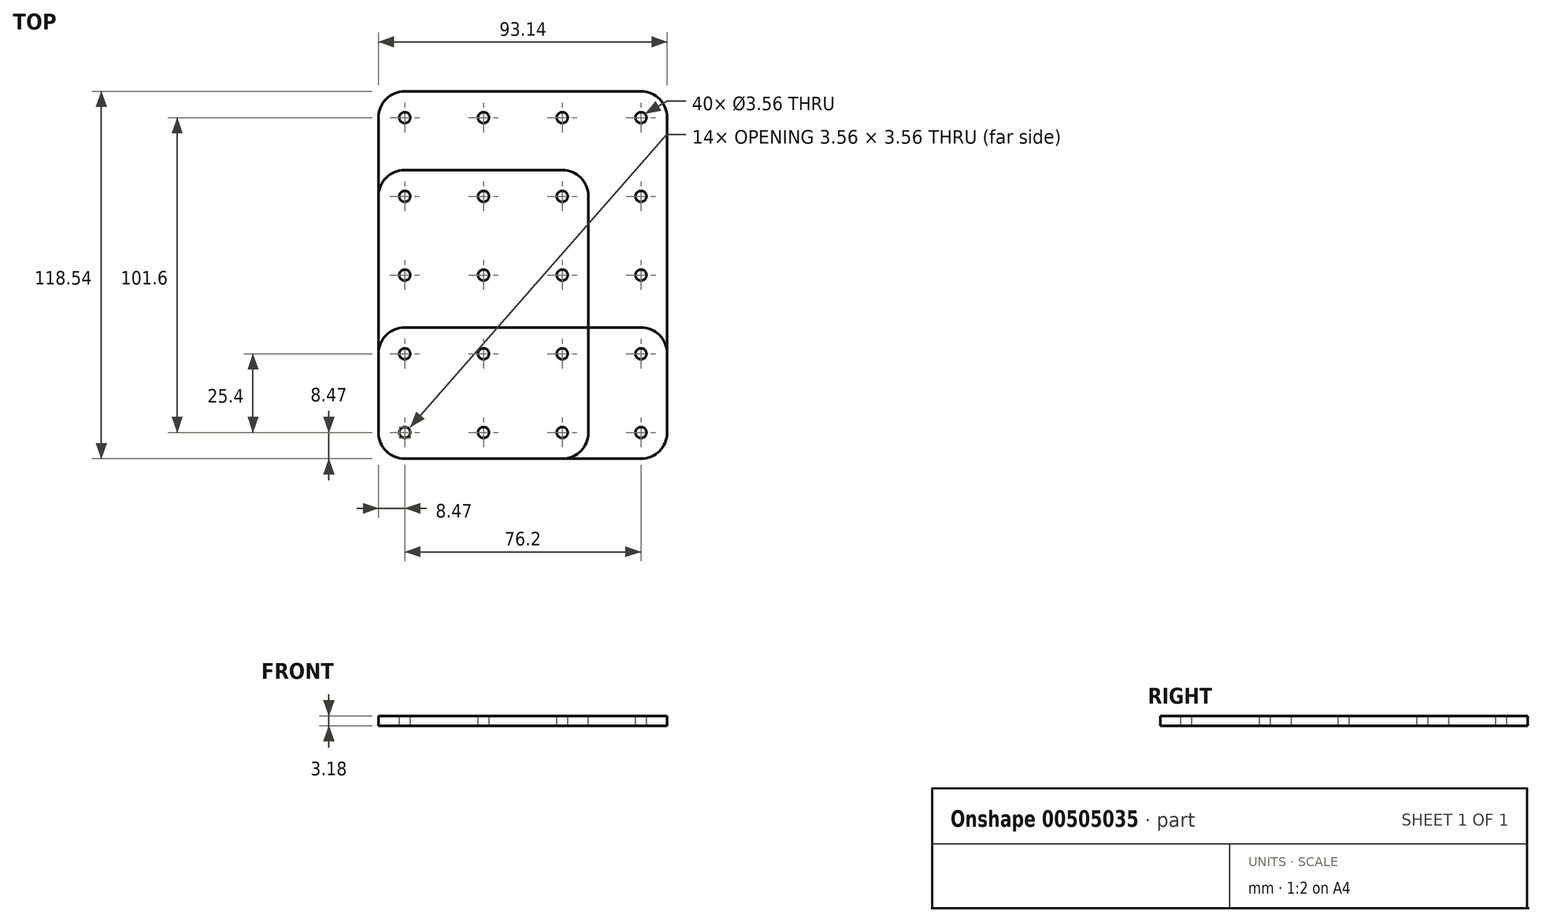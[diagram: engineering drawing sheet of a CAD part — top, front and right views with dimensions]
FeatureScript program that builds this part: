
annotation { "Feature Type Name" : "Feature", "Feature Type Description" : "" }
export const myFeature = defineFeature(function(context is Context, id is Id, definition is map)
    precondition{}
    {
        {
            var Q0;
            Q0=qCreatedBy(makeId("Front.planeOp"),FACE);
            var sketch = newSketch(context, id + "F0", { "sketchPlane" : qUnion([Q0])});
            skLineSegment(sketch, "E0", {"start": v(0, 0) * mm, "end": v(0, -3.18) * mm, "construction": true});
            skSolve(sketch);
        }
        {
            var Q0;
            Q0=qCreatedBy(makeId("Top.planeOp"),FACE);
            var sketch = newSketch(context, id + "F1", { "sketchPlane" : qUnion([Q0])});
            skCircle(sketch, "E1", {"center": v(0, 0) * mm, "radius": 1.78 * mm});
            skCircle(sketch, "E2", {"center": v(0, 0) * mm, "radius": 8.47 * mm, "construction": true});
            skCircle(sketch, "E3.0.1.0", {"center": v(0, 25.4) * mm, "radius": 1.78 * mm});
            skCircle(sketch, "E3.0.1.1", {"center": v(0, 25.4) * mm, "radius": 8.47 * mm, "construction": true});
            skCircle(sketch, "E3.1.0.0", {"center": v(25.4, 0) * mm, "radius": 1.78 * mm});
            skCircle(sketch, "E3.1.0.1", {"center": v(25.4, 0) * mm, "radius": 8.47 * mm, "construction": true});
            skCircle(sketch, "E3.1.1.0", {"center": v(25.4, 25.4) * mm, "radius": 1.78 * mm});
            skCircle(sketch, "E3.1.1.1", {"center": v(25.4, 25.4) * mm, "radius": 8.47 * mm, "construction": true});
            skCircle(sketch, "E3.2.0.0", {"center": v(50.8, 0) * mm, "radius": 1.78 * mm});
            skCircle(sketch, "E3.2.0.1", {"center": v(50.8, 0) * mm, "radius": 8.47 * mm, "construction": true});
            skCircle(sketch, "E3.2.1.0", {"center": v(50.8, 25.4) * mm, "radius": 1.78 * mm});
            skCircle(sketch, "E3.2.1.1", {"center": v(50.8, 25.4) * mm, "radius": 8.47 * mm, "construction": true});
            skCircle(sketch, "E3.3.0.0", {"center": v(76.2, 0) * mm, "radius": 1.78 * mm});
            skCircle(sketch, "E3.3.0.1", {"center": v(76.2, 0) * mm, "radius": 8.47 * mm, "construction": true});
            skCircle(sketch, "E3.3.1.0", {"center": v(76.2, 25.4) * mm, "radius": 1.78 * mm});
            skCircle(sketch, "E3.3.1.1", {"center": v(76.2, 25.4) * mm, "radius": 8.47 * mm, "construction": true});
            skLineSegment(sketch, "E3.direction1", {"start": v(0, 0) * mm, "end": v(25.4, 0) * mm, "construction": true});
            skLineSegment(sketch, "E3.direction2", {"start": v(0, 0) * mm, "end": v(0, 25.4) * mm, "construction": true});
            skLineSegment(sketch, "E4.bottom", {"start": v(0, 33.87) * mm, "end": v(76.2, 33.87) * mm});
            skLineSegment(sketch, "E4.top", {"start": v(0, -8.47) * mm, "end": v(76.2, -8.47) * mm});
            skLineSegment(sketch, "E4.left", {"start": v(-8.47, 25.4) * mm, "end": v(-8.47, 0) * mm});
            skLineSegment(sketch, "E4.right", {"start": v(84.67, 25.4) * mm, "end": v(84.67, 0) * mm});
            skPoint(sketch, "E5.visualSharp", {"position": v(-8.47, 33.87) * mm});
            skArc(sketch, "E5.filletArc", {"start": v(0, 33.87) * mm, "mid": v(-5.99, 31.39) * mm, "end": v(-8.47, 25.4) * mm});
            skPoint(sketch, "E6.visualSharp", {"position": v(84.67, 33.87) * mm});
            skArc(sketch, "E6.filletArc", {"start": v(84.67, 25.4) * mm, "mid": v(82.19, 31.39) * mm, "end": v(76.2, 33.87) * mm});
            skPoint(sketch, "E7.visualSharp", {"position": v(84.67, -8.47) * mm});
            skArc(sketch, "E7.filletArc", {"start": v(76.2, -8.47) * mm, "mid": v(82.19, -5.99) * mm, "end": v(84.67, 0) * mm});
            skPoint(sketch, "E8.visualSharp", {"position": v(-8.47, -8.47) * mm});
            skArc(sketch, "E8.filletArc", {"start": v(-8.47, 0) * mm, "mid": v(-5.99, -5.99) * mm, "end": v(0, -8.47) * mm});
            skSolve(sketch);
        }
        {
            var Q0;
            Q0=makeQuery(id+"F1.imprint","IMPRINT",FACE,{"disambiguationData":[TD([[makeQuery(id+"F1.imprint","IMPRINT",EDGE,{"derivedFrom":sQuery(id+"F1.wireOp",EDGE,"E1")}),-1.0]])]});
            var Q1;
            Q1=sQuery(id+"F0.wireOp",VERTEX,"E0.end");
            extrude(context, id + "F2", {"entities" : qUnion([Q0]), "endBound" : BoundingType.UP_TO_VERTEX, "oppositeDirection" : true, "endBoundEntityVertex" : qUnion([Q1]), "depth" : 25.4 * mm});
        }
        {
            var Q0;
            Q0=qCreatedBy(makeId("Top.planeOp"),FACE);
            var sketch = newSketch(context, id + "F3", { "sketchPlane" : qUnion([Q0])});
            skCircle(sketch, "E9", {"center": v(0, 0) * mm, "radius": 1.78 * mm});
            skCircle(sketch, "E10", {"center": v(0, 0) * mm, "radius": 8.47 * mm, "construction": true});
            skCircle(sketch, "E11.0.1.0", {"center": v(0, 25.4) * mm, "radius": 1.78 * mm});
            skCircle(sketch, "E11.0.1.1", {"center": v(0, 25.4) * mm, "radius": 8.47 * mm, "construction": true});
            skCircle(sketch, "E11.0.2.0", {"center": v(0, 50.8) * mm, "radius": 1.78 * mm});
            skCircle(sketch, "E11.0.2.1", {"center": v(0, 50.8) * mm, "radius": 8.47 * mm, "construction": true});
            skCircle(sketch, "E11.0.3.0", {"center": v(0, 76.2) * mm, "radius": 1.78 * mm});
            skCircle(sketch, "E11.0.3.1", {"center": v(0, 76.2) * mm, "radius": 8.47 * mm, "construction": true});
            skCircle(sketch, "E11.1.0.0", {"center": v(25.4, 0) * mm, "radius": 1.78 * mm});
            skCircle(sketch, "E11.1.0.1", {"center": v(25.4, 0) * mm, "radius": 8.47 * mm, "construction": true});
            skCircle(sketch, "E11.1.1.0", {"center": v(25.4, 25.4) * mm, "radius": 1.78 * mm});
            skCircle(sketch, "E11.1.1.1", {"center": v(25.4, 25.4) * mm, "radius": 8.47 * mm, "construction": true});
            skCircle(sketch, "E11.1.2.0", {"center": v(25.4, 50.8) * mm, "radius": 1.78 * mm});
            skCircle(sketch, "E11.1.2.1", {"center": v(25.4, 50.8) * mm, "radius": 8.47 * mm, "construction": true});
            skCircle(sketch, "E11.1.3.0", {"center": v(25.4, 76.2) * mm, "radius": 1.78 * mm});
            skCircle(sketch, "E11.1.3.1", {"center": v(25.4, 76.2) * mm, "radius": 8.47 * mm, "construction": true});
            skCircle(sketch, "E11.2.0.0", {"center": v(50.8, 0) * mm, "radius": 1.78 * mm});
            skCircle(sketch, "E11.2.0.1", {"center": v(50.8, 0) * mm, "radius": 8.47 * mm, "construction": true});
            skCircle(sketch, "E11.2.1.0", {"center": v(50.8, 25.4) * mm, "radius": 1.78 * mm});
            skCircle(sketch, "E11.2.1.1", {"center": v(50.8, 25.4) * mm, "radius": 8.47 * mm, "construction": true});
            skCircle(sketch, "E11.2.2.0", {"center": v(50.8, 50.8) * mm, "radius": 1.78 * mm});
            skCircle(sketch, "E11.2.2.1", {"center": v(50.8, 50.8) * mm, "radius": 8.47 * mm, "construction": true});
            skCircle(sketch, "E11.2.3.0", {"center": v(50.8, 76.2) * mm, "radius": 1.78 * mm});
            skCircle(sketch, "E11.2.3.1", {"center": v(50.8, 76.2) * mm, "radius": 8.47 * mm, "construction": true});
            skLineSegment(sketch, "E11.direction1", {"start": v(0, 0) * mm, "end": v(25.4, 0) * mm, "construction": true});
            skLineSegment(sketch, "E11.direction2", {"start": v(0, 0) * mm, "end": v(0, 25.4) * mm, "construction": true});
            skLineSegment(sketch, "E12.bottom", {"start": v(0, 84.67) * mm, "end": v(50.8, 84.67) * mm});
            skLineSegment(sketch, "E12.top", {"start": v(0, -8.47) * mm, "end": v(50.8, -8.47) * mm});
            skLineSegment(sketch, "E12.left", {"start": v(-8.47, 76.2) * mm, "end": v(-8.47, 0) * mm});
            skLineSegment(sketch, "E12.right", {"start": v(59.27, 76.2) * mm, "end": v(59.27, 0) * mm});
            skPoint(sketch, "E13.visualSharp", {"position": v(-8.47, 84.67) * mm});
            skArc(sketch, "E13.filletArc", {"start": v(0, 84.67) * mm, "mid": v(-5.99, 82.19) * mm, "end": v(-8.47, 76.2) * mm});
            skPoint(sketch, "E14.visualSharp", {"position": v(59.27, 84.67) * mm});
            skArc(sketch, "E14.filletArc", {"start": v(59.27, 76.2) * mm, "mid": v(56.79, 82.19) * mm, "end": v(50.8, 84.67) * mm});
            skPoint(sketch, "E15.visualSharp", {"position": v(59.27, -8.47) * mm});
            skArc(sketch, "E15.filletArc", {"start": v(50.8, -8.47) * mm, "mid": v(56.79, -5.99) * mm, "end": v(59.27, 0) * mm});
            skPoint(sketch, "E16.visualSharp", {"position": v(-8.47, -8.47) * mm});
            skArc(sketch, "E16.filletArc", {"start": v(-8.47, 0) * mm, "mid": v(-5.99, -5.99) * mm, "end": v(0, -8.47) * mm});
            skSolve(sketch);
        }
        {
            var Q0;
            Q0=makeQuery(id+"F3.imprint","IMPRINT",FACE,{"disambiguationData":[TD([[makeQuery(id+"F3.imprint","IMPRINT",EDGE,{"derivedFrom":sQuery(id+"F3.wireOp",EDGE,"E9")}),-1.0]])]});
            var Q1;
            Q1=sQuery(id+"F0.wireOp",VERTEX,"E0.end");
            extrude(context, id + "F4", {"entities" : qUnion([Q0]), "endBound" : BoundingType.UP_TO_VERTEX, "oppositeDirection" : true, "endBoundEntityVertex" : qUnion([Q1]), "depth" : 25.4 * mm});
        }
        {
            var Q0;
            Q0=qCreatedBy(makeId("Top.planeOp"),FACE);
            var sketch = newSketch(context, id + "F5", { "sketchPlane" : qUnion([Q0])});
            skCircle(sketch, "E17", {"center": v(0, 0) * mm, "radius": 1.78 * mm});
            skCircle(sketch, "E18", {"center": v(0, 0) * mm, "radius": 8.47 * mm, "construction": true});
            skCircle(sketch, "E19.0.1.0", {"center": v(0, 25.4) * mm, "radius": 1.78 * mm});
            skCircle(sketch, "E19.0.1.1", {"center": v(0, 25.4) * mm, "radius": 8.47 * mm, "construction": true});
            skCircle(sketch, "E19.0.2.0", {"center": v(0, 50.8) * mm, "radius": 1.78 * mm});
            skCircle(sketch, "E19.0.2.1", {"center": v(0, 50.8) * mm, "radius": 8.47 * mm, "construction": true});
            skCircle(sketch, "E19.0.3.0", {"center": v(0, 76.2) * mm, "radius": 1.78 * mm});
            skCircle(sketch, "E19.0.3.1", {"center": v(0, 76.2) * mm, "radius": 8.47 * mm, "construction": true});
            skCircle(sketch, "E19.0.4.0", {"center": v(0, 101.6) * mm, "radius": 1.78 * mm});
            skCircle(sketch, "E19.0.4.1", {"center": v(0, 101.6) * mm, "radius": 8.47 * mm, "construction": true});
            skCircle(sketch, "E19.1.0.0", {"center": v(25.4, 0) * mm, "radius": 1.78 * mm});
            skCircle(sketch, "E19.1.0.1", {"center": v(25.4, 0) * mm, "radius": 8.47 * mm, "construction": true});
            skCircle(sketch, "E19.1.1.0", {"center": v(25.4, 25.4) * mm, "radius": 1.78 * mm});
            skCircle(sketch, "E19.1.1.1", {"center": v(25.4, 25.4) * mm, "radius": 8.47 * mm, "construction": true});
            skCircle(sketch, "E19.1.2.0", {"center": v(25.4, 50.8) * mm, "radius": 1.78 * mm});
            skCircle(sketch, "E19.1.2.1", {"center": v(25.4, 50.8) * mm, "radius": 8.47 * mm, "construction": true});
            skCircle(sketch, "E19.1.3.0", {"center": v(25.4, 76.2) * mm, "radius": 1.78 * mm});
            skCircle(sketch, "E19.1.3.1", {"center": v(25.4, 76.2) * mm, "radius": 8.47 * mm, "construction": true});
            skCircle(sketch, "E19.1.4.0", {"center": v(25.4, 101.6) * mm, "radius": 1.78 * mm});
            skCircle(sketch, "E19.1.4.1", {"center": v(25.4, 101.6) * mm, "radius": 8.47 * mm, "construction": true});
            skCircle(sketch, "E19.2.0.0", {"center": v(50.8, 0) * mm, "radius": 1.78 * mm});
            skCircle(sketch, "E19.2.0.1", {"center": v(50.8, 0) * mm, "radius": 8.47 * mm, "construction": true});
            skCircle(sketch, "E19.2.1.0", {"center": v(50.8, 25.4) * mm, "radius": 1.78 * mm});
            skCircle(sketch, "E19.2.1.1", {"center": v(50.8, 25.4) * mm, "radius": 8.47 * mm, "construction": true});
            skCircle(sketch, "E19.2.2.0", {"center": v(50.8, 50.8) * mm, "radius": 1.78 * mm});
            skCircle(sketch, "E19.2.2.1", {"center": v(50.8, 50.8) * mm, "radius": 8.47 * mm, "construction": true});
            skCircle(sketch, "E19.2.3.0", {"center": v(50.8, 76.2) * mm, "radius": 1.78 * mm});
            skCircle(sketch, "E19.2.3.1", {"center": v(50.8, 76.2) * mm, "radius": 8.47 * mm, "construction": true});
            skCircle(sketch, "E19.2.4.0", {"center": v(50.8, 101.6) * mm, "radius": 1.78 * mm});
            skCircle(sketch, "E19.2.4.1", {"center": v(50.8, 101.6) * mm, "radius": 8.47 * mm, "construction": true});
            skCircle(sketch, "E19.3.0.0", {"center": v(76.2, 0) * mm, "radius": 1.78 * mm});
            skCircle(sketch, "E19.3.0.1", {"center": v(76.2, 0) * mm, "radius": 8.47 * mm, "construction": true});
            skCircle(sketch, "E19.3.1.0", {"center": v(76.2, 25.4) * mm, "radius": 1.78 * mm});
            skCircle(sketch, "E19.3.1.1", {"center": v(76.2, 25.4) * mm, "radius": 8.47 * mm, "construction": true});
            skCircle(sketch, "E19.3.2.0", {"center": v(76.2, 50.8) * mm, "radius": 1.78 * mm});
            skCircle(sketch, "E19.3.2.1", {"center": v(76.2, 50.8) * mm, "radius": 8.47 * mm, "construction": true});
            skCircle(sketch, "E19.3.3.0", {"center": v(76.2, 76.2) * mm, "radius": 1.78 * mm});
            skCircle(sketch, "E19.3.3.1", {"center": v(76.2, 76.2) * mm, "radius": 8.47 * mm, "construction": true});
            skCircle(sketch, "E19.3.4.0", {"center": v(76.2, 101.6) * mm, "radius": 1.78 * mm});
            skCircle(sketch, "E19.3.4.1", {"center": v(76.2, 101.6) * mm, "radius": 8.47 * mm, "construction": true});
            skLineSegment(sketch, "E19.direction1", {"start": v(0, 0) * mm, "end": v(25.4, 0) * mm, "construction": true});
            skLineSegment(sketch, "E19.direction2", {"start": v(0, 0) * mm, "end": v(0, 25.4) * mm, "construction": true});
            skLineSegment(sketch, "E20.bottom", {"start": v(0, 110.07) * mm, "end": v(76.2, 110.07) * mm});
            skLineSegment(sketch, "E20.top", {"start": v(0, -8.47) * mm, "end": v(76.2, -8.47) * mm});
            skLineSegment(sketch, "E20.left", {"start": v(-8.47, 101.6) * mm, "end": v(-8.47, 0) * mm});
            skLineSegment(sketch, "E20.right", {"start": v(84.67, 101.6) * mm, "end": v(84.67, 0) * mm});
            skPoint(sketch, "E21.visualSharp", {"position": v(-8.47, 110.07) * mm});
            skArc(sketch, "E21.filletArc", {"start": v(0, 110.07) * mm, "mid": v(-5.99, 107.59) * mm, "end": v(-8.47, 101.6) * mm});
            skPoint(sketch, "E22.visualSharp", {"position": v(84.67, 110.07) * mm});
            skArc(sketch, "E22.filletArc", {"start": v(84.67, 101.6) * mm, "mid": v(82.19, 107.59) * mm, "end": v(76.2, 110.07) * mm});
            skPoint(sketch, "E23.visualSharp", {"position": v(84.67, -8.47) * mm});
            skArc(sketch, "E23.filletArc", {"start": v(76.2, -8.47) * mm, "mid": v(82.19, -5.99) * mm, "end": v(84.67, 0) * mm});
            skPoint(sketch, "E24.visualSharp", {"position": v(-8.47, -8.47) * mm});
            skArc(sketch, "E24.filletArc", {"start": v(-8.47, 0) * mm, "mid": v(-5.99, -5.99) * mm, "end": v(0, -8.47) * mm});
            skSolve(sketch);
        }
        {
            var Q0;
            Q0=makeQuery(id+"F5.imprint","IMPRINT",FACE,{"disambiguationData":[TD([[makeQuery(id+"F5.imprint","IMPRINT",EDGE,{"derivedFrom":sQuery(id+"F5.wireOp",EDGE,"E17")}),-1.0]])]});
            var Q1;
            Q1=sQuery(id+"F0.wireOp",VERTEX,"E0.end");
            extrude(context, id + "F6", {"entities" : qUnion([Q0]), "endBound" : BoundingType.UP_TO_VERTEX, "oppositeDirection" : true, "endBoundEntityVertex" : qUnion([Q1]), "depth" : 25.4 * mm});
        }
    });
